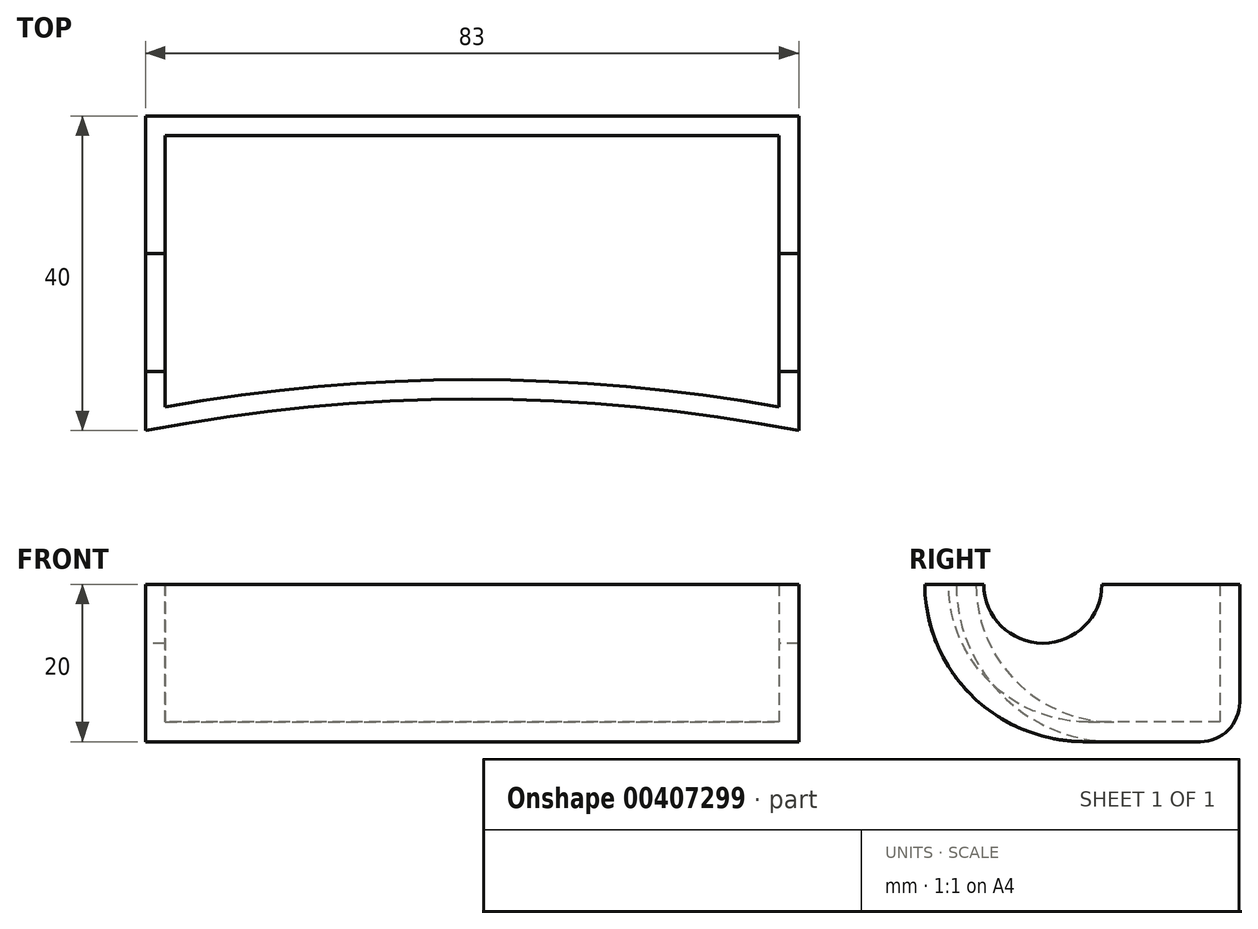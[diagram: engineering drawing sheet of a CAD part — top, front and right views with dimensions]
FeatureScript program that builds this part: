
annotation { "Feature Type Name" : "Feature", "Feature Type Description" : "" }
export const myFeature = defineFeature(function(context is Context, id is Id, definition is map)
    precondition{}
    {
        {
            var Q0;
            Q0=qCreatedBy(makeId("Top.planeOp"),FACE);
            var sketch = newSketch(context, id + "F0", { "sketchPlane" : qUnion([Q0])});
            skLineSegment(sketch, "E0.bottom", {"start": v(0, 0) * mm, "end": v(83, 0) * mm});
            skLineSegment(sketch, "E0.left", {"start": v(0, 0) * mm, "end": v(0, -40) * mm});
            skLineSegment(sketch, "E0.right", {"start": v(83, 0) * mm, "end": v(83, -40) * mm});
            skArc(sketch, "E1", {"start": v(83, -40) * mm, "mid": v(41.5, -36) * mm, "end": v(0, -40) * mm});
            skSolve(sketch);
        }
        {
            var Q0;
            Q0 = qSketchRegion(id + "F0", true);
            extrude(context, id + "F1", {"entities" : qUnion([Q0]), "depth" : 20 * mm});
        }
        {
            var Q0;
            Q0=makeQuery(id+"F1.opExtrude","CAP_EDGE",EDGE,{"disambiguationData":[OSD([sQuery(id+"F0.wireOp",EDGE,"E0.top")])],"isStart":true});
            var Q1;
            Q1=makeQuery(id+"F1.opExtrude","CAP_EDGE",EDGE,{"disambiguationData":[OSD([sQuery(id+"F0.wireOp",EDGE,"E1")])],"isStart":true});
            fillet(context, id + "F2", {"entities" : qUnion([Q0, Q1]), "radius" : 20 * mm, "tangentPropagation" : true, "allowEdgeOverflow" : false});
        }
        {
            var Q0;
            Q0=makeQuery(id+"F1.opExtrude","CAP_FACE",FACE,{"disambiguationData":[OSD([sQuery(id+"F0.wireOp",EDGE,"E0.bottom"),sQuery(id+"F0.wireOp",EDGE,"E0.top"),sQuery(id+"F0.wireOp",EDGE,"E0.left"),sQuery(id+"F0.wireOp",EDGE,"E0.right")])],"isStart":false});
            shell(context, id + "F3", {"entities" : qUnion([Q0]), "thickness" : 2.5 * mm});
        }
        {
            var Q0;
            Q0=makeQuery(id+"F1.opExtrude","CAP_EDGE",EDGE,{"disambiguationData":[OSD([sQuery(id+"F0.wireOp",EDGE,"E0.bottom")])],"isStart":true});
            fillet(context, id + "F4", {"entities" : qUnion([Q0]), "radius" : 5 * mm, "tangentPropagation" : true, "allowEdgeOverflow" : false});
        }
        {
            var Q0;
            Q0=qCreatedBy(makeId("Right.planeOp"),FACE);
            var sketch = newSketch(context, id + "F5", { "sketchPlane" : qUnion([Q0])});
            skLineSegment(sketch, "E2", {"start": v(0, 0) * mm, "end": v(0, 20) * mm});
            skLineSegment(sketch, "E3", {"start": v(0, 20) * mm, "end": v(-25, 20) * mm});
            skCircle(sketch, "E4", {"center": v(-25, 20) * mm, "radius": 7.5 * mm});
            skSolve(sketch);
        }
        {
            var Q0;
            Q0 = qSketchRegion(id + "F5", true);
            extrude(context, id + "F6", {"entities" : qUnion([Q0]), "operationType" : NewBodyOperationType.REMOVE, "depth" : 83 * mm});
        }
    });
